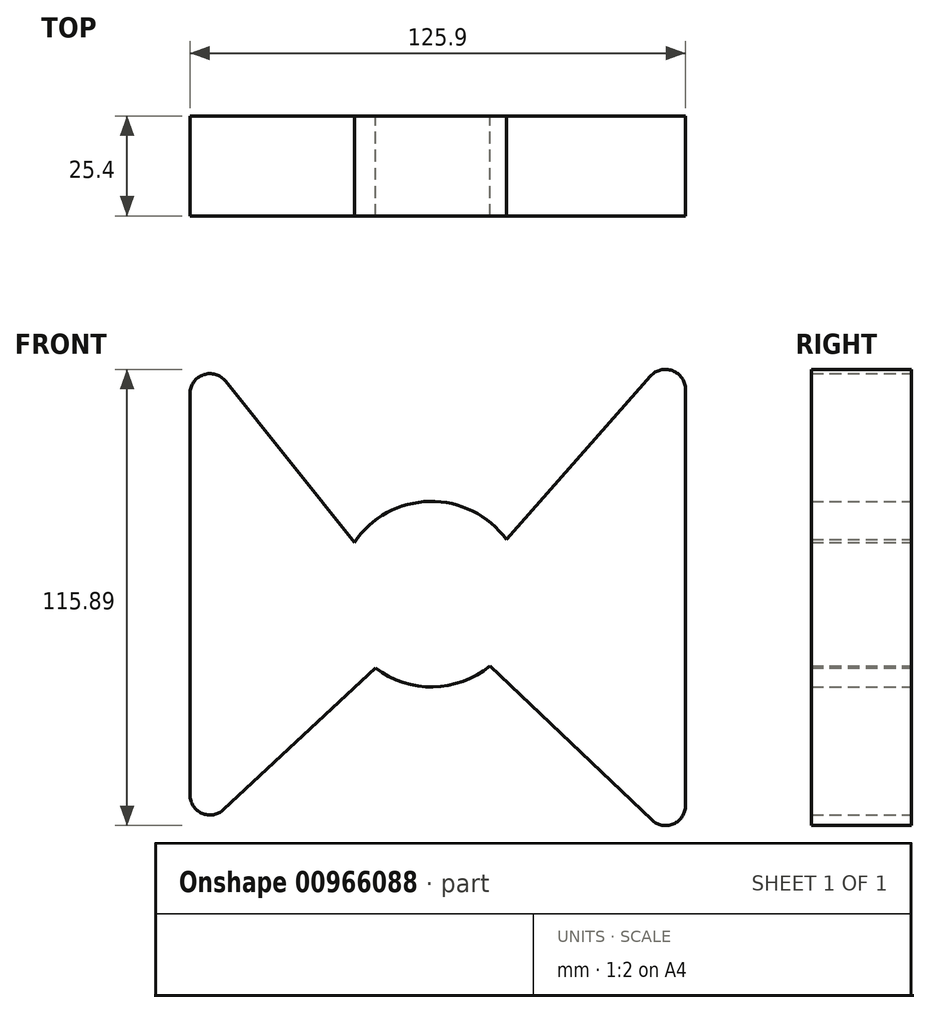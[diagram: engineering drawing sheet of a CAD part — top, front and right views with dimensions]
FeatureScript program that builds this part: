
annotation { "Feature Type Name" : "Feature", "Feature Type Description" : "" }
export const myFeature = defineFeature(function(context is Context, id is Id, definition is map)
    precondition{}
    {
        {
            var Q0;
            Q0=qCreatedBy(makeId("Front.planeOp"),FACE);
            var sketch = newSketch(context, id + "F0", { "sketchPlane" : qUnion([Q0])});
            skCircle(sketch, "E0", {"center": v(0, 0) * mm, "radius": 23.57 * mm});
            skLineSegment(sketch, "E1", {"start": v(14.92, -18.24) * mm, "end": v(64.57, -65.57) * mm});
            skLineSegment(sketch, "E2", {"start": v(64.57, -65.57) * mm, "end": v(64.57, 65.46) * mm});
            skLineSegment(sketch, "E3", {"start": v(64.57, 65.46) * mm, "end": v(19.05, 13.87) * mm});
            skLineSegment(sketch, "E4", {"start": v(-19.57, 13.14) * mm, "end": v(-61.33, 65.46) * mm});
            skLineSegment(sketch, "E5", {"start": v(-61.33, 65.46) * mm, "end": v(-61.33, -62.71) * mm});
            skLineSegment(sketch, "E6", {"start": v(-61.33, -62.71) * mm, "end": v(-14.23, -18.8) * mm});
            skSolve(sketch);
        }
        {
            var Q0;
            {var subQ0=sQuery(id+"F0.wireOp",EDGE,"E0");var subQ1=makeQuery(id+"F0.imprint","INTERSECT",VERTEX,{"derivedFrom":[subQ0,sQuery(id+"F0.wireOp",EDGE,"E3")]});Q0=makeQuery(id+"F0.imprint","IMPRINT",FACE,{"disambiguationData":[TD([[makeQuery(id+"F0.imprint","IMPRINT",EDGE,{"disambiguationData":[TD([[subQ1,-1.0]])],"derivedFrom":subQ0}),1.0]])]});}
            var Q1;
            {var subQ0=sQuery(id+"F0.wireOp",EDGE,"E1");Q1=makeQuery(id+"F0.imprint","IMPRINT",FACE,{"disambiguationData":[TD([[makeQuery(id+"F0.imprint","IMPRINT",EDGE,{"derivedFrom":subQ0}),1.0]])]});}
            var Q2;
            {var subQ0=sQuery(id+"F0.wireOp",EDGE,"E4");Q2=makeQuery(id+"F0.imprint","IMPRINT",FACE,{"disambiguationData":[TD([[makeQuery(id+"F0.imprint","IMPRINT",EDGE,{"derivedFrom":subQ0}),1.0]])]});}
            extrude(context, id + "F1", {"entities" : qUnion([Q0, Q1, Q2]), "depth" : 25.4 * mm, "offsetDistance" : 25.4 * mm});
        }
        {
            var Q0;
            Q0=makeQuery(id+"F1.opExtrude","SWEPT_EDGE",EDGE,{"disambiguationData":[OSD([sQuery(id+"F0.wireOp",EDGE,"E4"),sQuery(id+"F0.wireOp",EDGE,"E5")])]});
            var Q1;
            Q1=makeQuery(id+"F1.opExtrude","SWEPT_EDGE",EDGE,{"disambiguationData":[OSD([sQuery(id+"F0.wireOp",EDGE,"E2"),sQuery(id+"F0.wireOp",EDGE,"E3")])]});
            var Q2;
            Q2=makeQuery(id+"F1.opExtrude","SWEPT_EDGE",EDGE,{"disambiguationData":[OSD([sQuery(id+"F0.wireOp",EDGE,"E1"),sQuery(id+"F0.wireOp",EDGE,"E2")])]});
            var Q3;
            Q3=makeQuery(id+"F1.opExtrude","SWEPT_EDGE",EDGE,{"disambiguationData":[OSD([sQuery(id+"F0.wireOp",EDGE,"E5"),sQuery(id+"F0.wireOp",EDGE,"E6")])]});
            fillet(context, id + "F2", {"entities" : qUnion([Q0, Q1, Q2, Q3]), "radius" : 5.08 * mm, "tangentPropagation" : true, "allowEdgeOverflow" : false});
        }
    });
